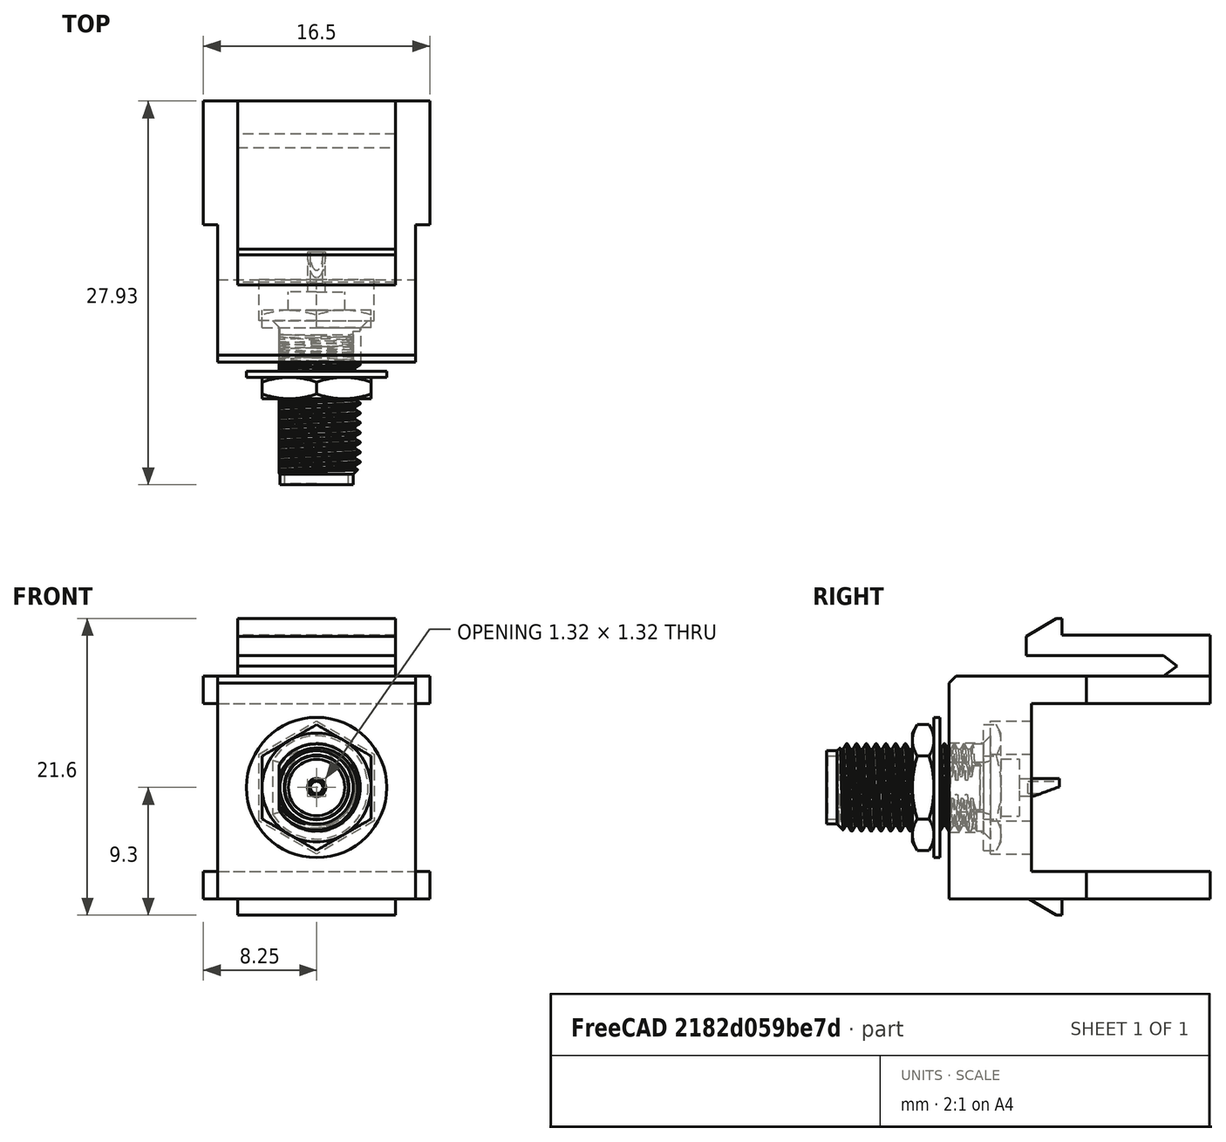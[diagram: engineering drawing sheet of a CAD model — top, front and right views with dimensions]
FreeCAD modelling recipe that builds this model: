
FCSTD DOCUMENT  (FreeCAD 1.0R39319 (Git))
Label: SMA_Keystone
License: All rights reserved
LicenseURL: https://en.wikipedia.org/wiki/All_rights_reserved
objects: Part::Feature×2, Sketcher::SketchObject×2, App::FeaturePython×2, PartDesign::FeatureBase×1, PartDesign::Pocket×1, PartDesign::Pad×1, PartDesign::Chamfer×1, PartDesign::Body×1, App::Part×1, Assembly::JointGroup×1, Assembly::AssemblyObject×1
note: 18 computed .brp shape members not serialized (recipe doc carries the construction recipe); baked Part::Feature solids carry a one-line shape summary decoded from their .brp

FEATURE [Part::Feature] keystone_blank_insert_chamfer002_solid  label="keystone_blank_insert_chamfer002 (Solid)"
  shape: bbox 16.5 x 19 x 21.6 mm, 39 faces (baked)
FEATURE [PartDesign::FeatureBase] BaseFeature
  BaseFeature = -> keystone_blank_insert_chamfer002_solid
  Suppressed = false
FEATURE [Sketcher::SketchObject] Sketch
  ArcFitTolerance = 1e-06
  AttachmentSupport = -> [BaseFeature]
  ExternalGeometry = -> [BaseFeature]
  FullyConstrained = true
  MakeInternals = false
  MapMode = 5
  Placement = pos=(0,3,0) rot=(0,0.707107,0.707107;3.14159rad)
  expr: Constraints[6] = 6.5 / 2
  sketch-geometry (4):
    g0: LineSegment [constr] StartX=0 StartY=14.2 StartZ=0 EndX=-14.4 EndY=2 EndZ=0
    g1: GeomPoint [constr] X=-7.2 Y=8.1 Z=0
    g2: LineSegment StartX=-4.5 StartY=9.90901 StartZ=0 EndX=-4.5 EndY=6.29099 EndZ=0
    g3: ArcOfCircle CenterX=-7.2 CenterY=8.1 CenterZ=0 NormalX=0 NormalY=0 NormalZ=1 AngleXU=0 Radius=3.25 StartAngle=0.590308 EndAngle=5.69288
  constraints (9):
    c: Coincident(g0,g-4)
    c: Symmetric(g0,g0,g1)
    c: Vertical(g2)
    c: Coincident(g3,g1)
    c: Coincident(g3,g2)
    c: Coincident(g3,g2)
    c: Radius(g3) = 3.25
    c: Distance(g3,g2) = -0.55
    c: Coincident(g0,g-5)
FEATURE [PartDesign::Pocket] Pocket
  BaseFeature = -> BaseFeature
  Direction = (0,-1,2e-16)
  Length = 5
  Length2 = 5
  Profile = -> Sketch
  ReferenceAxis = -> Sketch [N_Axis]
  Refine = true
  Suppressed = false
  Type = 1
FEATURE [Sketcher::SketchObject] Sketch001
  ArcFitTolerance = 1e-06
  AttachmentSupport = -> [Pocket]
  ExternalGeometry = -> [Sketch,Pocket]
  FullyConstrained = true
  MakeInternals = false
  MapMode = 5
  Placement = pos=(0,3,0) rot=(0,0.707107,0.707107;3.14159rad)
  sketch-geometry (11):
    g0: LineSegment StartX=-3 StartY=5.67513 StartZ=0 EndX=-3 EndY=10.5249 EndZ=0
    g1: LineSegment StartX=-3 StartY=10.5249 StartZ=0 EndX=-7.2 EndY=12.9497 EndZ=0
    g2: LineSegment StartX=-7.2 StartY=12.9497 StartZ=0 EndX=-11.4 EndY=10.5249 EndZ=0
    g3: LineSegment StartX=-11.4 StartY=10.5249 StartZ=0 EndX=-11.4 EndY=5.67513 EndZ=0
    g4: LineSegment StartX=-11.4 StartY=5.67513 StartZ=0 EndX=-7.2 EndY=3.25026 EndZ=0
    g5: LineSegment StartX=-7.2 StartY=3.25026 StartZ=0 EndX=-3 EndY=5.67513 EndZ=0
    g6: Circle [constr] CenterX=-7.2 CenterY=8.1 CenterZ=0 NormalX=0 NormalY=0 NormalZ=1 AngleXU=0 Radius=4.84974
    g7: LineSegment StartX=0 StartY=14.2 StartZ=0 EndX=-14.4 EndY=14.2 EndZ=0
    g8: LineSegment StartX=-14.4 StartY=14.2 StartZ=0 EndX=-14.4 EndY=2 EndZ=0
    g9: LineSegment StartX=-14.4 StartY=2 StartZ=0 EndX=0 EndY=2 EndZ=0
    g10: LineSegment StartX=0 StartY=2 StartZ=0 EndX=0 EndY=14.2 EndZ=0
  constraints (26):
    c: Coincident(g0,g1)
    c: Coincident(g1,g2)
    c: Coincident(g2,g3)
    c: Coincident(g3,g4)
    c: Coincident(g4,g5)
    c: Coincident(g5,g0)
    c: Equal(g0, g1-g5) x5
    c: PointOnObject(g0,g6)
    c: PointOnObject(g1,g6)
    c: PointOnObject(g2,g6)
    c: PointOnObject(g3,g6)
    c: PointOnObject(g4,g6)
    c: PointOnObject(g5,g6)
    c: Vertical(g0)
    c: Distance(g0,g3) = 8.4
    c: Coincident(g6,g-3)
    c: Coincident(g7,g8)
    c: Coincident(g8,g9)
    c: Coincident(g9,g10)
    c: Coincident(g10,g7)
    c: Horizontal(g7)
    c: Horizontal(g9)
    c: Vertical(g8)
    c: Vertical(g10)
    c: Coincident(g7,g-4)
    c: Coincident(g8,g-5)
FEATURE [PartDesign::Pad] Pad
  BaseFeature = -> Pocket
  Direction = (0,1,-2e-16)
  Length = 3
  Length2 = 10
  Profile = -> Sketch001
  ReferenceAxis = -> Sketch001 [N_Axis]
  Refine = true
  Suppressed = false
  Type = 0
FEATURE [PartDesign::Chamfer] Chamfer
  Angle = 45
  Base = -> Pad [Edge79,Edge82]
  BaseFeature = -> Pad
  ChamferType = 0
  FlipDirection = false
  Refine = true
  Size = 0.5
  Size2 = 1
  SupportTransform = false
  Suppressed = false
  UseAllEdges = false
FEATURE [PartDesign::Body] Body
  AllowCompound = false
  BaseFeature = -> keystone_blank_insert_chamfer002_solid
  Group = -> [BaseFeature,Sketch,Pocket,Sketch001,Pad,Chamfer]
  Origin = -> Origin
  Tip = -> Chamfer
FEATURE [App::Part] Part  label="Keystone"
  Group = -> [keystone_blank_insert_chamfer002_solid,Body]
  Origin = -> Origin001
FEATURE [App::FeaturePython] GroundedJoint  # Assembly grounded joint (typed FeaturePython)
  ObjectToGround = -> Part
FEATURE [Part::Feature] Part__Feature  label="1053072-1"
  Placement = pos=(7.2,-8.93,8.1) rot=(0,-0.707107,0.707107;3.14159rad)
  shape: bbox 10.21 x 16.97 x 10.21 mm, 172 faces (baked)
FEATURE [App::FeaturePython] Joint  label="Fixed"  # Assembly joint (typed FeaturePython)
  Activated = true
  AngleMax = 0
  AngleMin = 0
  Detach1 = false
  Detach2 = false
  Distance = 0
  Distance2 = 0
  EnableAngleMax = false
  EnableAngleMin = false
  EnableLengthMax = false
  EnableLengthMin = false
  JointType = 0 (Fixed)
  LengthMax = 0
  LengthMin = 0
  Offset2 = pos=(0,0,0) rot=(0,0,-1;1.5708rad)
  Placement1 = pos=(7.2,2.5,8.1) rot=(0,0.707107,0.707107;3.14159rad)
  Placement2 = pos=(0,1.8e-15,-11.43) rot=(-1,0,0;3.14159rad)
  Reference1 = -> Assembly [Part.Body.Face1,Part.Body.Edge2]
  Reference2 = -> Assembly [Part__Feature.Edge80,Part__Feature.Edge80]
FEATURE [Assembly::JointGroup] Joints
  Group = -> [GroundedJoint,Joint]
FEATURE [Assembly::AssemblyObject] Assembly  label="SMA Keystone"
  Group = -> [Joints,Part,GroundedJoint,Part__Feature,Joint]
  Origin = -> Origin004
  Type = Assembly
